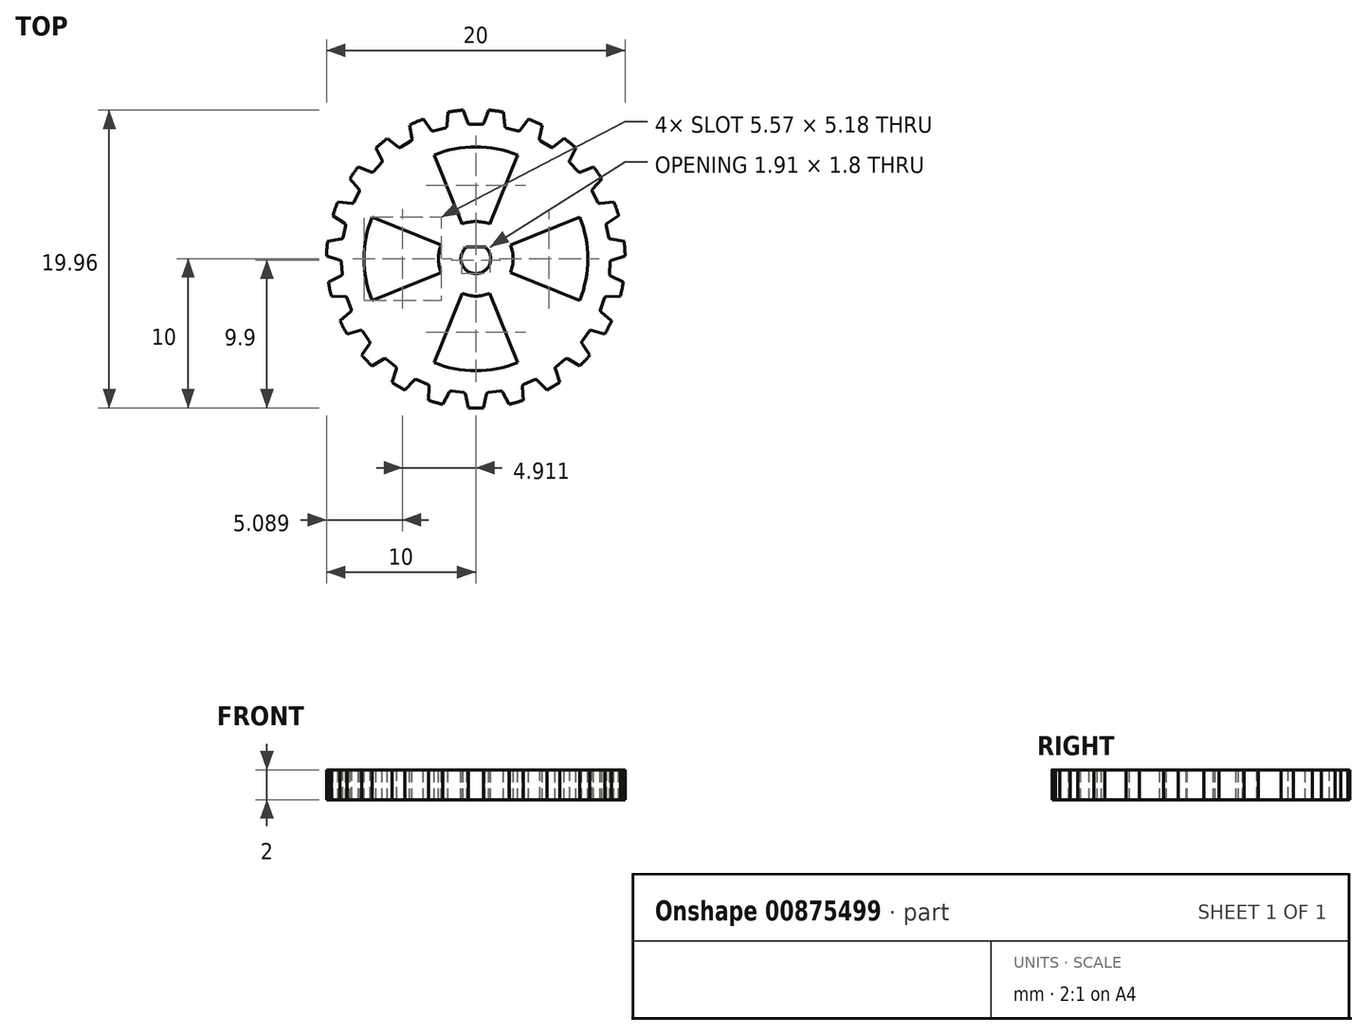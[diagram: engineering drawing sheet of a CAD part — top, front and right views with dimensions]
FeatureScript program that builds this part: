
annotation { "Feature Type Name" : "Feature", "Feature Type Description" : "" }
export const myFeature = defineFeature(function(context is Context, id is Id, definition is map)
    precondition{}
    {
        {
            var Q0;
            Q0=qCreatedBy(makeId("Top.planeOp"),FACE);
            var sketch = newSketch(context, id + "F0", { "sketchPlane" : qUnion([Q0])});
            skCircle(sketch, "E0", {"center": v(0, 0) * mm, "radius": 10 * mm});
            skSolve(sketch);
        }
        {
            var Q0;
            Q0=qSketchRegion(id+"F0",true);
            extrude(context, id + "F1", {"entities" : qUnion([Q0]), "depth" : 2 * mm, "offsetDistance" : 25 * mm});
        }
        {
            var Q0;
            Q0=makeQuery(id+"F1.opExtrude","CAP_FACE",FACE,{"disambiguationData":[OSD([sQuery(id+"F0.wireOp",EDGE,"E0")])],"isStart":false});
            var sketch = newSketch(context, id + "F2", { "sketchPlane" : qUnion([Q0])});
            skLineSegment(sketch, "E1", {"start": v(0, 0) * mm, "end": v(0, 9) * mm});
            skLineSegment(sketch, "E2", {"start": v(0, 9) * mm, "end": v(0.5, 9) * mm});
            skLineSegment(sketch, "E3", {"start": v(0, 9) * mm, "end": v(0, 10) * mm});
            skLineSegment(sketch, "E4", {"start": v(0, 10) * mm, "end": v(0.88, 10) * mm});
            skLineSegment(sketch, "E5", {"start": v(0.88, 10) * mm, "end": v(0.5, 9) * mm});
            skLineSegment(sketch, "E6.MirrorCS", {"start": v(0, 10) * mm, "end": v(-0.88, 10) * mm});
            skLineSegment(sketch, "E7.MirrorCS", {"start": v(-0.88, 10) * mm, "end": v(-0.5, 9) * mm});
            skLineSegment(sketch, "E8.MirrorCS", {"start": v(0, 9) * mm, "end": v(-0.5, 9) * mm});
            skSolve(sketch);
        }
        {
            var Q0;
            {var subQ0=sQuery(id+"F2.wireOp",EDGE,"E2");Q0=makeQuery(id+"F2.imprint","IMPRINT",FACE,{"disambiguationData":[TD([[makeQuery(id+"F2.imprint","IMPRINT",EDGE,{"derivedFrom":subQ0}),1.0]])]});}
            var Q1;
            {var subQ0=sQuery(id+"F2.wireOp",EDGE,"E3");Q1=makeQuery(id+"F2.imprint","IMPRINT",FACE,{"disambiguationData":[TD([[makeQuery(id+"F2.imprint","IMPRINT",EDGE,{"derivedFrom":subQ0}),1.0]])]});}
            extrude(context, id + "F3", {"entities" : qUnion([Q0, Q1]), "operationType" : NewBodyOperationType.REMOVE, "oppositeDirection" : true, "depth" : 25 * mm, "offsetDistance" : 25 * mm});
        }
        {
            var Q0;
            Q0=makeQuery(id+"F3.boolean.opBoolean","COPY",FACE,{"derivedFrom":makeQuery(id+"F3.opExtrude","SWEPT_FACE",FACE,{"disambiguationData":[OSD([sQuery(id+"F2.wireOp",EDGE,"E5")])]})});
            var Q1;
            Q1=makeQuery(id+"F3.boolean.opBoolean","COPY",FACE,{"derivedFrom":makeQuery(id+"F3.opExtrude","SWEPT_FACE",FACE,{"disambiguationData":[OSD([sQuery(id+"F2.wireOp",EDGE,"E2"),sQuery(id+"F2.wireOp",EDGE,"E8.MirrorCS")])]})});
            var Q2;
            Q2=makeQuery(id+"F3.boolean.opBoolean","COPY",FACE,{"derivedFrom":makeQuery(id+"F3.opExtrude","SWEPT_FACE",FACE,{"disambiguationData":[OSD([sQuery(id+"F2.wireOp",EDGE,"E7.MirrorCS")])]})});
            var Q3;
            Q3=makeQuery(id+"F1.opExtrude","SWEPT_FACE",FACE,{"disambiguationData":[OSD([sQuery(id+"F0.wireOp",EDGE,"E0")])]});
            circularPattern(context, id + "F4", {"patternType" : PatternType.FACE, "faces" : qUnion([Q0, Q1, Q2]), "axis" : qUnion([Q3]), "angle" : 360 * degree, "instanceCount" : 23, "equalSpace" : true});
        }
        {
            var Q0;
            Q0=makeQuery(id+"F3.boolean.opBoolean","COPY",EDGE,{"derivedFrom":makeQuery(id+"F3.opExtrude","SWEPT_EDGE",EDGE,{"disambiguationData":[OSD([sQuery(id+"F2.wireOp",EDGE,"E2"),sQuery(id+"F2.wireOp",EDGE,"E5")])]})});
            var Q1;
            Q1=makeQuery(id+"F3.boolean.opBoolean","COPY",EDGE,{"derivedFrom":makeQuery(id+"F3.opExtrude","SWEPT_EDGE",EDGE,{"disambiguationData":[OSD([sQuery(id+"F2.wireOp",EDGE,"E7.MirrorCS"),sQuery(id+"F2.wireOp",EDGE,"E8.MirrorCS")])]})});
            var Q2;
            Q2=makeQuery(id+"F3.boolean.opBoolean","COPY",EDGE,{"derivedFrom":makeQuery(id+"F3.opExtrude","SWEPT_EDGE",EDGE,{"disambiguationData":[OSD([sQuery(id+"F0.wireOp",EDGE,"E0"),sQuery(id+"F2.wireOp",EDGE,"E5")])]})});
            var Q3;
            Q3=makeQuery(id+"F3.boolean.opBoolean","COPY",EDGE,{"derivedFrom":makeQuery(id+"F3.opExtrude","SWEPT_EDGE",EDGE,{"disambiguationData":[OSD([sQuery(id+"F0.wireOp",EDGE,"E0"),sQuery(id+"F2.wireOp",EDGE,"E7.MirrorCS")])]})});
            fillet(context, id + "F5", {"entities" : qUnion([Q0, Q1, Q2, Q3]), "radius" : .15 * mm, "tangentPropagation" : true, "allowEdgeOverflow" : false});
        }
        {
            var Q0;
            Q0=makeQuery(id+"F4.opPattern","COPY",EDGE,{"derivedFrom":makeQuery(id+"F3.boolean.opBoolean","COPY",EDGE,{"derivedFrom":makeQuery(id+"F3.opExtrude","SWEPT_EDGE",EDGE,{"disambiguationData":[OSD([sQuery(id+"F0.wireOp",EDGE,"E0"),sQuery(id+"F2.wireOp",EDGE,"E5")])]})}),"instanceName":"22"});
            var Q1;
            Q1=makeQuery(id+"F4.opPattern","COPY",EDGE,{"derivedFrom":makeQuery(id+"F3.boolean.opBoolean","COPY",EDGE,{"derivedFrom":makeQuery(id+"F3.opExtrude","SWEPT_EDGE",EDGE,{"disambiguationData":[OSD([sQuery(id+"F2.wireOp",EDGE,"E2"),sQuery(id+"F2.wireOp",EDGE,"E5")])]})}),"instanceName":"22"});
            var Q2;
            Q2=makeQuery(id+"F4.opPattern","COPY",EDGE,{"derivedFrom":makeQuery(id+"F3.boolean.opBoolean","COPY",EDGE,{"derivedFrom":makeQuery(id+"F3.opExtrude","SWEPT_EDGE",EDGE,{"disambiguationData":[OSD([sQuery(id+"F2.wireOp",EDGE,"E7.MirrorCS"),sQuery(id+"F2.wireOp",EDGE,"E8.MirrorCS")])]})}),"instanceName":"22"});
            var Q3;
            Q3=makeQuery(id+"F4.opPattern","COPY",EDGE,{"derivedFrom":makeQuery(id+"F3.boolean.opBoolean","COPY",EDGE,{"derivedFrom":makeQuery(id+"F3.opExtrude","SWEPT_EDGE",EDGE,{"disambiguationData":[OSD([sQuery(id+"F0.wireOp",EDGE,"E0"),sQuery(id+"F2.wireOp",EDGE,"E7.MirrorCS")])]})}),"instanceName":"22"});
            var Q4;
            Q4=makeQuery(id+"F4.opPattern","COPY",EDGE,{"derivedFrom":makeQuery(id+"F3.boolean.opBoolean","COPY",EDGE,{"derivedFrom":makeQuery(id+"F3.opExtrude","SWEPT_EDGE",EDGE,{"disambiguationData":[OSD([sQuery(id+"F0.wireOp",EDGE,"E0"),sQuery(id+"F2.wireOp",EDGE,"E5")])]})}),"instanceName":"21"});
            var Q5;
            Q5=makeQuery(id+"F4.opPattern","COPY",EDGE,{"derivedFrom":makeQuery(id+"F3.boolean.opBoolean","COPY",EDGE,{"derivedFrom":makeQuery(id+"F3.opExtrude","SWEPT_EDGE",EDGE,{"disambiguationData":[OSD([sQuery(id+"F2.wireOp",EDGE,"E2"),sQuery(id+"F2.wireOp",EDGE,"E5")])]})}),"instanceName":"21"});
            var Q6;
            Q6=makeQuery(id+"F4.opPattern","COPY",EDGE,{"derivedFrom":makeQuery(id+"F3.boolean.opBoolean","COPY",EDGE,{"derivedFrom":makeQuery(id+"F3.opExtrude","SWEPT_EDGE",EDGE,{"disambiguationData":[OSD([sQuery(id+"F2.wireOp",EDGE,"E7.MirrorCS"),sQuery(id+"F2.wireOp",EDGE,"E8.MirrorCS")])]})}),"instanceName":"21"});
            var Q7;
            Q7=makeQuery(id+"F4.opPattern","COPY",EDGE,{"derivedFrom":makeQuery(id+"F3.boolean.opBoolean","COPY",EDGE,{"derivedFrom":makeQuery(id+"F3.opExtrude","SWEPT_EDGE",EDGE,{"disambiguationData":[OSD([sQuery(id+"F0.wireOp",EDGE,"E0"),sQuery(id+"F2.wireOp",EDGE,"E7.MirrorCS")])]})}),"instanceName":"21"});
            var Q8;
            Q8=makeQuery(id+"F4.opPattern","COPY",EDGE,{"derivedFrom":makeQuery(id+"F3.boolean.opBoolean","COPY",EDGE,{"derivedFrom":makeQuery(id+"F3.opExtrude","SWEPT_EDGE",EDGE,{"disambiguationData":[OSD([sQuery(id+"F0.wireOp",EDGE,"E0"),sQuery(id+"F2.wireOp",EDGE,"E5")])]})}),"instanceName":"20"});
            var Q9;
            Q9=makeQuery(id+"F4.opPattern","COPY",EDGE,{"derivedFrom":makeQuery(id+"F3.boolean.opBoolean","COPY",EDGE,{"derivedFrom":makeQuery(id+"F3.opExtrude","SWEPT_EDGE",EDGE,{"disambiguationData":[OSD([sQuery(id+"F2.wireOp",EDGE,"E2"),sQuery(id+"F2.wireOp",EDGE,"E5")])]})}),"instanceName":"20"});
            var Q10;
            Q10=makeQuery(id+"F4.opPattern","COPY",EDGE,{"derivedFrom":makeQuery(id+"F3.boolean.opBoolean","COPY",EDGE,{"derivedFrom":makeQuery(id+"F3.opExtrude","SWEPT_EDGE",EDGE,{"disambiguationData":[OSD([sQuery(id+"F2.wireOp",EDGE,"E7.MirrorCS"),sQuery(id+"F2.wireOp",EDGE,"E8.MirrorCS")])]})}),"instanceName":"20"});
            var Q11;
            Q11=makeQuery(id+"F4.opPattern","COPY",EDGE,{"derivedFrom":makeQuery(id+"F3.boolean.opBoolean","COPY",EDGE,{"derivedFrom":makeQuery(id+"F3.opExtrude","SWEPT_EDGE",EDGE,{"disambiguationData":[OSD([sQuery(id+"F0.wireOp",EDGE,"E0"),sQuery(id+"F2.wireOp",EDGE,"E7.MirrorCS")])]})}),"instanceName":"20"});
            var Q12;
            Q12=makeQuery(id+"F4.opPattern","COPY",EDGE,{"derivedFrom":makeQuery(id+"F3.boolean.opBoolean","COPY",EDGE,{"derivedFrom":makeQuery(id+"F3.opExtrude","SWEPT_EDGE",EDGE,{"disambiguationData":[OSD([sQuery(id+"F0.wireOp",EDGE,"E0"),sQuery(id+"F2.wireOp",EDGE,"E5")])]})}),"instanceName":"19"});
            var Q13;
            Q13=makeQuery(id+"F4.opPattern","COPY",EDGE,{"derivedFrom":makeQuery(id+"F3.boolean.opBoolean","COPY",EDGE,{"derivedFrom":makeQuery(id+"F3.opExtrude","SWEPT_EDGE",EDGE,{"disambiguationData":[OSD([sQuery(id+"F2.wireOp",EDGE,"E2"),sQuery(id+"F2.wireOp",EDGE,"E5")])]})}),"instanceName":"19"});
            var Q14;
            Q14=makeQuery(id+"F4.opPattern","COPY",EDGE,{"derivedFrom":makeQuery(id+"F3.boolean.opBoolean","COPY",EDGE,{"derivedFrom":makeQuery(id+"F3.opExtrude","SWEPT_EDGE",EDGE,{"disambiguationData":[OSD([sQuery(id+"F2.wireOp",EDGE,"E7.MirrorCS"),sQuery(id+"F2.wireOp",EDGE,"E8.MirrorCS")])]})}),"instanceName":"19"});
            var Q15;
            Q15=makeQuery(id+"F4.opPattern","COPY",EDGE,{"derivedFrom":makeQuery(id+"F3.boolean.opBoolean","COPY",EDGE,{"derivedFrom":makeQuery(id+"F3.opExtrude","SWEPT_EDGE",EDGE,{"disambiguationData":[OSD([sQuery(id+"F0.wireOp",EDGE,"E0"),sQuery(id+"F2.wireOp",EDGE,"E7.MirrorCS")])]})}),"instanceName":"19"});
            fillet(context, id + "F6", {"entities" : qUnion([Q0, Q1, Q2, Q3, Q4, Q5, Q6, Q7, Q8, Q9, Q10, Q11, Q12, Q13, Q14, Q15]), "radius" : .15 * mm, "tangentPropagation" : true, "allowEdgeOverflow" : false});
        }
        {
            var Q0;
            Q0=makeQuery(id+"F4.opPattern","COPY",EDGE,{"derivedFrom":makeQuery(id+"F3.boolean.opBoolean","COPY",EDGE,{"derivedFrom":makeQuery(id+"F3.opExtrude","SWEPT_EDGE",EDGE,{"disambiguationData":[OSD([sQuery(id+"F0.wireOp",EDGE,"E0"),sQuery(id+"F2.wireOp",EDGE,"E7.MirrorCS")])]})}),"instanceName":"1"});
            var Q1;
            Q1=makeQuery(id+"F4.opPattern","COPY",EDGE,{"derivedFrom":makeQuery(id+"F3.boolean.opBoolean","COPY",EDGE,{"derivedFrom":makeQuery(id+"F3.opExtrude","SWEPT_EDGE",EDGE,{"disambiguationData":[OSD([sQuery(id+"F2.wireOp",EDGE,"E7.MirrorCS"),sQuery(id+"F2.wireOp",EDGE,"E8.MirrorCS")])]})}),"instanceName":"1"});
            var Q2;
            Q2=makeQuery(id+"F4.opPattern","COPY",EDGE,{"derivedFrom":makeQuery(id+"F3.boolean.opBoolean","COPY",EDGE,{"derivedFrom":makeQuery(id+"F3.opExtrude","SWEPT_EDGE",EDGE,{"disambiguationData":[OSD([sQuery(id+"F2.wireOp",EDGE,"E2"),sQuery(id+"F2.wireOp",EDGE,"E5")])]})}),"instanceName":"1"});
            var Q3;
            Q3=makeQuery(id+"F4.opPattern","COPY",EDGE,{"derivedFrom":makeQuery(id+"F3.boolean.opBoolean","COPY",EDGE,{"derivedFrom":makeQuery(id+"F3.opExtrude","SWEPT_EDGE",EDGE,{"disambiguationData":[OSD([sQuery(id+"F0.wireOp",EDGE,"E0"),sQuery(id+"F2.wireOp",EDGE,"E5")])]})}),"instanceName":"1"});
            var Q4;
            Q4=makeQuery(id+"F4.opPattern","COPY",EDGE,{"derivedFrom":makeQuery(id+"F3.boolean.opBoolean","COPY",EDGE,{"derivedFrom":makeQuery(id+"F3.opExtrude","SWEPT_EDGE",EDGE,{"disambiguationData":[OSD([sQuery(id+"F0.wireOp",EDGE,"E0"),sQuery(id+"F2.wireOp",EDGE,"E7.MirrorCS")])]})}),"instanceName":"2"});
            var Q5;
            Q5=makeQuery(id+"F4.opPattern","COPY",EDGE,{"derivedFrom":makeQuery(id+"F3.boolean.opBoolean","COPY",EDGE,{"derivedFrom":makeQuery(id+"F3.opExtrude","SWEPT_EDGE",EDGE,{"disambiguationData":[OSD([sQuery(id+"F2.wireOp",EDGE,"E2"),sQuery(id+"F2.wireOp",EDGE,"E5")])]})}),"instanceName":"2"});
            var Q6;
            Q6=makeQuery(id+"F4.opPattern","COPY",EDGE,{"derivedFrom":makeQuery(id+"F3.boolean.opBoolean","COPY",EDGE,{"derivedFrom":makeQuery(id+"F3.opExtrude","SWEPT_EDGE",EDGE,{"disambiguationData":[OSD([sQuery(id+"F2.wireOp",EDGE,"E7.MirrorCS"),sQuery(id+"F2.wireOp",EDGE,"E8.MirrorCS")])]})}),"instanceName":"2"});
            var Q7;
            Q7=makeQuery(id+"F4.opPattern","COPY",EDGE,{"derivedFrom":makeQuery(id+"F3.boolean.opBoolean","COPY",EDGE,{"derivedFrom":makeQuery(id+"F3.opExtrude","SWEPT_EDGE",EDGE,{"disambiguationData":[OSD([sQuery(id+"F0.wireOp",EDGE,"E0"),sQuery(id+"F2.wireOp",EDGE,"E5")])]})}),"instanceName":"2"});
            var Q8;
            Q8=makeQuery(id+"F4.opPattern","COPY",EDGE,{"derivedFrom":makeQuery(id+"F3.boolean.opBoolean","COPY",EDGE,{"derivedFrom":makeQuery(id+"F3.opExtrude","SWEPT_EDGE",EDGE,{"disambiguationData":[OSD([sQuery(id+"F0.wireOp",EDGE,"E0"),sQuery(id+"F2.wireOp",EDGE,"E7.MirrorCS")])]})}),"instanceName":"3"});
            var Q9;
            Q9=makeQuery(id+"F4.opPattern","COPY",EDGE,{"derivedFrom":makeQuery(id+"F3.boolean.opBoolean","COPY",EDGE,{"derivedFrom":makeQuery(id+"F3.opExtrude","SWEPT_EDGE",EDGE,{"disambiguationData":[OSD([sQuery(id+"F2.wireOp",EDGE,"E7.MirrorCS"),sQuery(id+"F2.wireOp",EDGE,"E8.MirrorCS")])]})}),"instanceName":"3"});
            var Q10;
            Q10=makeQuery(id+"F4.opPattern","COPY",EDGE,{"derivedFrom":makeQuery(id+"F3.boolean.opBoolean","COPY",EDGE,{"derivedFrom":makeQuery(id+"F3.opExtrude","SWEPT_EDGE",EDGE,{"disambiguationData":[OSD([sQuery(id+"F2.wireOp",EDGE,"E2"),sQuery(id+"F2.wireOp",EDGE,"E5")])]})}),"instanceName":"3"});
            var Q11;
            Q11=makeQuery(id+"F4.opPattern","COPY",EDGE,{"derivedFrom":makeQuery(id+"F3.boolean.opBoolean","COPY",EDGE,{"derivedFrom":makeQuery(id+"F3.opExtrude","SWEPT_EDGE",EDGE,{"disambiguationData":[OSD([sQuery(id+"F0.wireOp",EDGE,"E0"),sQuery(id+"F2.wireOp",EDGE,"E5")])]})}),"instanceName":"3"});
            var Q12;
            Q12=makeQuery(id+"F4.opPattern","COPY",EDGE,{"derivedFrom":makeQuery(id+"F3.boolean.opBoolean","COPY",EDGE,{"derivedFrom":makeQuery(id+"F3.opExtrude","SWEPT_EDGE",EDGE,{"disambiguationData":[OSD([sQuery(id+"F0.wireOp",EDGE,"E0"),sQuery(id+"F2.wireOp",EDGE,"E7.MirrorCS")])]})}),"instanceName":"4"});
            var Q13;
            Q13=makeQuery(id+"F4.opPattern","COPY",EDGE,{"derivedFrom":makeQuery(id+"F3.boolean.opBoolean","COPY",EDGE,{"derivedFrom":makeQuery(id+"F3.opExtrude","SWEPT_EDGE",EDGE,{"disambiguationData":[OSD([sQuery(id+"F2.wireOp",EDGE,"E7.MirrorCS"),sQuery(id+"F2.wireOp",EDGE,"E8.MirrorCS")])]})}),"instanceName":"4"});
            var Q14;
            Q14=makeQuery(id+"F4.opPattern","COPY",EDGE,{"derivedFrom":makeQuery(id+"F3.boolean.opBoolean","COPY",EDGE,{"derivedFrom":makeQuery(id+"F3.opExtrude","SWEPT_EDGE",EDGE,{"disambiguationData":[OSD([sQuery(id+"F2.wireOp",EDGE,"E2"),sQuery(id+"F2.wireOp",EDGE,"E5")])]})}),"instanceName":"4"});
            var Q15;
            Q15=makeQuery(id+"F4.opPattern","COPY",EDGE,{"derivedFrom":makeQuery(id+"F3.boolean.opBoolean","COPY",EDGE,{"derivedFrom":makeQuery(id+"F3.opExtrude","SWEPT_EDGE",EDGE,{"disambiguationData":[OSD([sQuery(id+"F0.wireOp",EDGE,"E0"),sQuery(id+"F2.wireOp",EDGE,"E5")])]})}),"instanceName":"4"});
            var Q16;
            Q16=makeQuery(id+"F4.opPattern","COPY",EDGE,{"derivedFrom":makeQuery(id+"F3.boolean.opBoolean","COPY",EDGE,{"derivedFrom":makeQuery(id+"F3.opExtrude","SWEPT_EDGE",EDGE,{"disambiguationData":[OSD([sQuery(id+"F0.wireOp",EDGE,"E0"),sQuery(id+"F2.wireOp",EDGE,"E7.MirrorCS")])]})}),"instanceName":"5"});
            var Q17;
            Q17=makeQuery(id+"F4.opPattern","COPY",EDGE,{"derivedFrom":makeQuery(id+"F3.boolean.opBoolean","COPY",EDGE,{"derivedFrom":makeQuery(id+"F3.opExtrude","SWEPT_EDGE",EDGE,{"disambiguationData":[OSD([sQuery(id+"F2.wireOp",EDGE,"E7.MirrorCS"),sQuery(id+"F2.wireOp",EDGE,"E8.MirrorCS")])]})}),"instanceName":"5"});
            var Q18;
            Q18=makeQuery(id+"F4.opPattern","COPY",EDGE,{"derivedFrom":makeQuery(id+"F3.boolean.opBoolean","COPY",EDGE,{"derivedFrom":makeQuery(id+"F3.opExtrude","SWEPT_EDGE",EDGE,{"disambiguationData":[OSD([sQuery(id+"F2.wireOp",EDGE,"E2"),sQuery(id+"F2.wireOp",EDGE,"E5")])]})}),"instanceName":"5"});
            var Q19;
            Q19=makeQuery(id+"F4.opPattern","COPY",EDGE,{"derivedFrom":makeQuery(id+"F3.boolean.opBoolean","COPY",EDGE,{"derivedFrom":makeQuery(id+"F3.opExtrude","SWEPT_EDGE",EDGE,{"disambiguationData":[OSD([sQuery(id+"F0.wireOp",EDGE,"E0"),sQuery(id+"F2.wireOp",EDGE,"E5")])]})}),"instanceName":"5"});
            var Q20;
            Q20=makeQuery(id+"F4.opPattern","COPY",EDGE,{"derivedFrom":makeQuery(id+"F3.boolean.opBoolean","COPY",EDGE,{"derivedFrom":makeQuery(id+"F3.opExtrude","SWEPT_EDGE",EDGE,{"disambiguationData":[OSD([sQuery(id+"F0.wireOp",EDGE,"E0"),sQuery(id+"F2.wireOp",EDGE,"E7.MirrorCS")])]})}),"instanceName":"6"});
            var Q21;
            Q21=makeQuery(id+"F4.opPattern","COPY",EDGE,{"derivedFrom":makeQuery(id+"F3.boolean.opBoolean","COPY",EDGE,{"derivedFrom":makeQuery(id+"F3.opExtrude","SWEPT_EDGE",EDGE,{"disambiguationData":[OSD([sQuery(id+"F2.wireOp",EDGE,"E7.MirrorCS"),sQuery(id+"F2.wireOp",EDGE,"E8.MirrorCS")])]})}),"instanceName":"6"});
            var Q22;
            Q22=makeQuery(id+"F4.opPattern","COPY",EDGE,{"derivedFrom":makeQuery(id+"F3.boolean.opBoolean","COPY",EDGE,{"derivedFrom":makeQuery(id+"F3.opExtrude","SWEPT_EDGE",EDGE,{"disambiguationData":[OSD([sQuery(id+"F2.wireOp",EDGE,"E2"),sQuery(id+"F2.wireOp",EDGE,"E5")])]})}),"instanceName":"6"});
            var Q23;
            Q23=makeQuery(id+"F4.opPattern","COPY",EDGE,{"derivedFrom":makeQuery(id+"F3.boolean.opBoolean","COPY",EDGE,{"derivedFrom":makeQuery(id+"F3.opExtrude","SWEPT_EDGE",EDGE,{"disambiguationData":[OSD([sQuery(id+"F0.wireOp",EDGE,"E0"),sQuery(id+"F2.wireOp",EDGE,"E5")])]})}),"instanceName":"6"});
            var Q24;
            Q24=makeQuery(id+"F4.opPattern","COPY",EDGE,{"derivedFrom":makeQuery(id+"F3.boolean.opBoolean","COPY",EDGE,{"derivedFrom":makeQuery(id+"F3.opExtrude","SWEPT_EDGE",EDGE,{"disambiguationData":[OSD([sQuery(id+"F0.wireOp",EDGE,"E0"),sQuery(id+"F2.wireOp",EDGE,"E7.MirrorCS")])]})}),"instanceName":"7"});
            var Q25;
            Q25=makeQuery(id+"F4.opPattern","COPY",EDGE,{"derivedFrom":makeQuery(id+"F3.boolean.opBoolean","COPY",EDGE,{"derivedFrom":makeQuery(id+"F3.opExtrude","SWEPT_EDGE",EDGE,{"disambiguationData":[OSD([sQuery(id+"F2.wireOp",EDGE,"E7.MirrorCS"),sQuery(id+"F2.wireOp",EDGE,"E8.MirrorCS")])]})}),"instanceName":"7"});
            fillet(context, id + "F7", {"entities" : qUnion([Q0, Q1, Q2, Q3, Q4, Q5, Q6, Q7, Q8, Q9, Q10, Q11, Q12, Q13, Q14, Q15, Q16, Q17, Q18, Q19, Q20, Q21, Q22, Q23, Q24, Q25]), "radius" : .15 * mm, "tangentPropagation" : true, "allowEdgeOverflow" : false});
        }
        {
            var Q0;
            Q0=makeQuery(id+"F4.opPattern","COPY",EDGE,{"derivedFrom":makeQuery(id+"F3.boolean.opBoolean","COPY",EDGE,{"derivedFrom":makeQuery(id+"F3.opExtrude","SWEPT_EDGE",EDGE,{"disambiguationData":[OSD([sQuery(id+"F2.wireOp",EDGE,"E2"),sQuery(id+"F2.wireOp",EDGE,"E5")])]})}),"instanceName":"7"});
            var Q1;
            Q1=makeQuery(id+"F4.opPattern","COPY",EDGE,{"derivedFrom":makeQuery(id+"F3.boolean.opBoolean","COPY",EDGE,{"derivedFrom":makeQuery(id+"F3.opExtrude","SWEPT_EDGE",EDGE,{"disambiguationData":[OSD([sQuery(id+"F0.wireOp",EDGE,"E0"),sQuery(id+"F2.wireOp",EDGE,"E5")])]})}),"instanceName":"7"});
            var Q2;
            Q2=makeQuery(id+"F4.opPattern","COPY",EDGE,{"derivedFrom":makeQuery(id+"F3.boolean.opBoolean","COPY",EDGE,{"derivedFrom":makeQuery(id+"F3.opExtrude","SWEPT_EDGE",EDGE,{"disambiguationData":[OSD([sQuery(id+"F0.wireOp",EDGE,"E0"),sQuery(id+"F2.wireOp",EDGE,"E7.MirrorCS")])]})}),"instanceName":"8"});
            var Q3;
            Q3=makeQuery(id+"F4.opPattern","COPY",EDGE,{"derivedFrom":makeQuery(id+"F3.boolean.opBoolean","COPY",EDGE,{"derivedFrom":makeQuery(id+"F3.opExtrude","SWEPT_EDGE",EDGE,{"disambiguationData":[OSD([sQuery(id+"F2.wireOp",EDGE,"E7.MirrorCS"),sQuery(id+"F2.wireOp",EDGE,"E8.MirrorCS")])]})}),"instanceName":"8"});
            var Q4;
            Q4=makeQuery(id+"F4.opPattern","COPY",EDGE,{"derivedFrom":makeQuery(id+"F3.boolean.opBoolean","COPY",EDGE,{"derivedFrom":makeQuery(id+"F3.opExtrude","SWEPT_EDGE",EDGE,{"disambiguationData":[OSD([sQuery(id+"F2.wireOp",EDGE,"E2"),sQuery(id+"F2.wireOp",EDGE,"E5")])]})}),"instanceName":"8"});
            var Q5;
            Q5=makeQuery(id+"F4.opPattern","COPY",EDGE,{"derivedFrom":makeQuery(id+"F3.boolean.opBoolean","COPY",EDGE,{"derivedFrom":makeQuery(id+"F3.opExtrude","SWEPT_EDGE",EDGE,{"disambiguationData":[OSD([sQuery(id+"F0.wireOp",EDGE,"E0"),sQuery(id+"F2.wireOp",EDGE,"E5")])]})}),"instanceName":"8"});
            var Q6;
            Q6=makeQuery(id+"F4.opPattern","COPY",EDGE,{"derivedFrom":makeQuery(id+"F3.boolean.opBoolean","COPY",EDGE,{"derivedFrom":makeQuery(id+"F3.opExtrude","SWEPT_EDGE",EDGE,{"disambiguationData":[OSD([sQuery(id+"F0.wireOp",EDGE,"E0"),sQuery(id+"F2.wireOp",EDGE,"E7.MirrorCS")])]})}),"instanceName":"9"});
            var Q7;
            Q7=makeQuery(id+"F4.opPattern","COPY",EDGE,{"derivedFrom":makeQuery(id+"F3.boolean.opBoolean","COPY",EDGE,{"derivedFrom":makeQuery(id+"F3.opExtrude","SWEPT_EDGE",EDGE,{"disambiguationData":[OSD([sQuery(id+"F2.wireOp",EDGE,"E7.MirrorCS"),sQuery(id+"F2.wireOp",EDGE,"E8.MirrorCS")])]})}),"instanceName":"9"});
            var Q8;
            Q8=makeQuery(id+"F4.opPattern","COPY",EDGE,{"derivedFrom":makeQuery(id+"F3.boolean.opBoolean","COPY",EDGE,{"derivedFrom":makeQuery(id+"F3.opExtrude","SWEPT_EDGE",EDGE,{"disambiguationData":[OSD([sQuery(id+"F2.wireOp",EDGE,"E2"),sQuery(id+"F2.wireOp",EDGE,"E5")])]})}),"instanceName":"9"});
            var Q9;
            Q9=makeQuery(id+"F4.opPattern","COPY",EDGE,{"derivedFrom":makeQuery(id+"F3.boolean.opBoolean","COPY",EDGE,{"derivedFrom":makeQuery(id+"F3.opExtrude","SWEPT_EDGE",EDGE,{"disambiguationData":[OSD([sQuery(id+"F0.wireOp",EDGE,"E0"),sQuery(id+"F2.wireOp",EDGE,"E5")])]})}),"instanceName":"9"});
            var Q10;
            Q10=makeQuery(id+"F4.opPattern","COPY",EDGE,{"derivedFrom":makeQuery(id+"F3.boolean.opBoolean","COPY",EDGE,{"derivedFrom":makeQuery(id+"F3.opExtrude","SWEPT_EDGE",EDGE,{"disambiguationData":[OSD([sQuery(id+"F0.wireOp",EDGE,"E0"),sQuery(id+"F2.wireOp",EDGE,"E7.MirrorCS")])]})}),"instanceName":"10"});
            var Q11;
            Q11=makeQuery(id+"F4.opPattern","COPY",EDGE,{"derivedFrom":makeQuery(id+"F3.boolean.opBoolean","COPY",EDGE,{"derivedFrom":makeQuery(id+"F3.opExtrude","SWEPT_EDGE",EDGE,{"disambiguationData":[OSD([sQuery(id+"F2.wireOp",EDGE,"E7.MirrorCS"),sQuery(id+"F2.wireOp",EDGE,"E8.MirrorCS")])]})}),"instanceName":"10"});
            var Q12;
            Q12=makeQuery(id+"F4.opPattern","COPY",EDGE,{"derivedFrom":makeQuery(id+"F3.boolean.opBoolean","COPY",EDGE,{"derivedFrom":makeQuery(id+"F3.opExtrude","SWEPT_EDGE",EDGE,{"disambiguationData":[OSD([sQuery(id+"F2.wireOp",EDGE,"E2"),sQuery(id+"F2.wireOp",EDGE,"E5")])]})}),"instanceName":"10"});
            var Q13;
            Q13=makeQuery(id+"F4.opPattern","COPY",EDGE,{"derivedFrom":makeQuery(id+"F3.boolean.opBoolean","COPY",EDGE,{"derivedFrom":makeQuery(id+"F3.opExtrude","SWEPT_EDGE",EDGE,{"disambiguationData":[OSD([sQuery(id+"F0.wireOp",EDGE,"E0"),sQuery(id+"F2.wireOp",EDGE,"E5")])]})}),"instanceName":"10"});
            var Q14;
            Q14=makeQuery(id+"F4.opPattern","COPY",EDGE,{"derivedFrom":makeQuery(id+"F3.boolean.opBoolean","COPY",EDGE,{"derivedFrom":makeQuery(id+"F3.opExtrude","SWEPT_EDGE",EDGE,{"disambiguationData":[OSD([sQuery(id+"F0.wireOp",EDGE,"E0"),sQuery(id+"F2.wireOp",EDGE,"E7.MirrorCS")])]})}),"instanceName":"11"});
            var Q15;
            Q15=makeQuery(id+"F4.opPattern","COPY",EDGE,{"derivedFrom":makeQuery(id+"F3.boolean.opBoolean","COPY",EDGE,{"derivedFrom":makeQuery(id+"F3.opExtrude","SWEPT_EDGE",EDGE,{"disambiguationData":[OSD([sQuery(id+"F2.wireOp",EDGE,"E7.MirrorCS"),sQuery(id+"F2.wireOp",EDGE,"E8.MirrorCS")])]})}),"instanceName":"11"});
            var Q16;
            Q16=makeQuery(id+"F4.opPattern","COPY",EDGE,{"derivedFrom":makeQuery(id+"F3.boolean.opBoolean","COPY",EDGE,{"derivedFrom":makeQuery(id+"F3.opExtrude","SWEPT_EDGE",EDGE,{"disambiguationData":[OSD([sQuery(id+"F0.wireOp",EDGE,"E0"),sQuery(id+"F2.wireOp",EDGE,"E5")])]})}),"instanceName":"11"});
            var Q17;
            Q17=makeQuery(id+"F4.opPattern","COPY",EDGE,{"derivedFrom":makeQuery(id+"F3.boolean.opBoolean","COPY",EDGE,{"derivedFrom":makeQuery(id+"F3.opExtrude","SWEPT_EDGE",EDGE,{"disambiguationData":[OSD([sQuery(id+"F2.wireOp",EDGE,"E2"),sQuery(id+"F2.wireOp",EDGE,"E5")])]})}),"instanceName":"11"});
            var Q18;
            Q18=makeQuery(id+"F4.opPattern","COPY",EDGE,{"derivedFrom":makeQuery(id+"F3.boolean.opBoolean","COPY",EDGE,{"derivedFrom":makeQuery(id+"F3.opExtrude","SWEPT_EDGE",EDGE,{"disambiguationData":[OSD([sQuery(id+"F0.wireOp",EDGE,"E0"),sQuery(id+"F2.wireOp",EDGE,"E7.MirrorCS")])]})}),"instanceName":"12"});
            var Q19;
            Q19=makeQuery(id+"F4.opPattern","COPY",EDGE,{"derivedFrom":makeQuery(id+"F3.boolean.opBoolean","COPY",EDGE,{"derivedFrom":makeQuery(id+"F3.opExtrude","SWEPT_EDGE",EDGE,{"disambiguationData":[OSD([sQuery(id+"F2.wireOp",EDGE,"E7.MirrorCS"),sQuery(id+"F2.wireOp",EDGE,"E8.MirrorCS")])]})}),"instanceName":"12"});
            var Q20;
            Q20=makeQuery(id+"F4.opPattern","COPY",EDGE,{"derivedFrom":makeQuery(id+"F3.boolean.opBoolean","COPY",EDGE,{"derivedFrom":makeQuery(id+"F3.opExtrude","SWEPT_EDGE",EDGE,{"disambiguationData":[OSD([sQuery(id+"F2.wireOp",EDGE,"E2"),sQuery(id+"F2.wireOp",EDGE,"E5")])]})}),"instanceName":"12"});
            var Q21;
            Q21=makeQuery(id+"F4.opPattern","COPY",EDGE,{"derivedFrom":makeQuery(id+"F3.boolean.opBoolean","COPY",EDGE,{"derivedFrom":makeQuery(id+"F3.opExtrude","SWEPT_EDGE",EDGE,{"disambiguationData":[OSD([sQuery(id+"F0.wireOp",EDGE,"E0"),sQuery(id+"F2.wireOp",EDGE,"E5")])]})}),"instanceName":"12"});
            var Q22;
            Q22=makeQuery(id+"F4.opPattern","COPY",EDGE,{"derivedFrom":makeQuery(id+"F3.boolean.opBoolean","COPY",EDGE,{"derivedFrom":makeQuery(id+"F3.opExtrude","SWEPT_EDGE",EDGE,{"disambiguationData":[OSD([sQuery(id+"F0.wireOp",EDGE,"E0"),sQuery(id+"F2.wireOp",EDGE,"E7.MirrorCS")])]})}),"instanceName":"13"});
            var Q23;
            Q23=makeQuery(id+"F4.opPattern","COPY",EDGE,{"derivedFrom":makeQuery(id+"F3.boolean.opBoolean","COPY",EDGE,{"derivedFrom":makeQuery(id+"F3.opExtrude","SWEPT_EDGE",EDGE,{"disambiguationData":[OSD([sQuery(id+"F2.wireOp",EDGE,"E7.MirrorCS"),sQuery(id+"F2.wireOp",EDGE,"E8.MirrorCS")])]})}),"instanceName":"13"});
            var Q24;
            Q24=makeQuery(id+"F4.opPattern","COPY",EDGE,{"derivedFrom":makeQuery(id+"F3.boolean.opBoolean","COPY",EDGE,{"derivedFrom":makeQuery(id+"F3.opExtrude","SWEPT_EDGE",EDGE,{"disambiguationData":[OSD([sQuery(id+"F0.wireOp",EDGE,"E0"),sQuery(id+"F2.wireOp",EDGE,"E5")])]})}),"instanceName":"13"});
            var Q25;
            Q25=makeQuery(id+"F4.opPattern","COPY",EDGE,{"derivedFrom":makeQuery(id+"F3.boolean.opBoolean","COPY",EDGE,{"derivedFrom":makeQuery(id+"F3.opExtrude","SWEPT_EDGE",EDGE,{"disambiguationData":[OSD([sQuery(id+"F0.wireOp",EDGE,"E0"),sQuery(id+"F2.wireOp",EDGE,"E7.MirrorCS")])]})}),"instanceName":"14"});
            var Q26;
            Q26=makeQuery(id+"F4.opPattern","COPY",EDGE,{"derivedFrom":makeQuery(id+"F3.boolean.opBoolean","COPY",EDGE,{"derivedFrom":makeQuery(id+"F3.opExtrude","SWEPT_EDGE",EDGE,{"disambiguationData":[OSD([sQuery(id+"F2.wireOp",EDGE,"E7.MirrorCS"),sQuery(id+"F2.wireOp",EDGE,"E8.MirrorCS")])]})}),"instanceName":"14"});
            var Q27;
            Q27=makeQuery(id+"F4.opPattern","COPY",EDGE,{"derivedFrom":makeQuery(id+"F3.boolean.opBoolean","COPY",EDGE,{"derivedFrom":makeQuery(id+"F3.opExtrude","SWEPT_EDGE",EDGE,{"disambiguationData":[OSD([sQuery(id+"F2.wireOp",EDGE,"E2"),sQuery(id+"F2.wireOp",EDGE,"E5")])]})}),"instanceName":"14"});
            var Q28;
            Q28=makeQuery(id+"F4.opPattern","COPY",EDGE,{"derivedFrom":makeQuery(id+"F3.boolean.opBoolean","COPY",EDGE,{"derivedFrom":makeQuery(id+"F3.opExtrude","SWEPT_EDGE",EDGE,{"disambiguationData":[OSD([sQuery(id+"F0.wireOp",EDGE,"E0"),sQuery(id+"F2.wireOp",EDGE,"E5")])]})}),"instanceName":"14"});
            var Q29;
            Q29=makeQuery(id+"F4.opPattern","COPY",EDGE,{"derivedFrom":makeQuery(id+"F3.boolean.opBoolean","COPY",EDGE,{"derivedFrom":makeQuery(id+"F3.opExtrude","SWEPT_EDGE",EDGE,{"disambiguationData":[OSD([sQuery(id+"F0.wireOp",EDGE,"E0"),sQuery(id+"F2.wireOp",EDGE,"E7.MirrorCS")])]})}),"instanceName":"15"});
            var Q30;
            Q30=makeQuery(id+"F4.opPattern","COPY",EDGE,{"derivedFrom":makeQuery(id+"F3.boolean.opBoolean","COPY",EDGE,{"derivedFrom":makeQuery(id+"F3.opExtrude","SWEPT_EDGE",EDGE,{"disambiguationData":[OSD([sQuery(id+"F2.wireOp",EDGE,"E2"),sQuery(id+"F2.wireOp",EDGE,"E5")])]})}),"instanceName":"15"});
            var Q31;
            Q31=makeQuery(id+"F4.opPattern","COPY",EDGE,{"derivedFrom":makeQuery(id+"F3.boolean.opBoolean","COPY",EDGE,{"derivedFrom":makeQuery(id+"F3.opExtrude","SWEPT_EDGE",EDGE,{"disambiguationData":[OSD([sQuery(id+"F0.wireOp",EDGE,"E0"),sQuery(id+"F2.wireOp",EDGE,"E5")])]})}),"instanceName":"15"});
            var Q32;
            Q32=makeQuery(id+"F4.opPattern","COPY",EDGE,{"derivedFrom":makeQuery(id+"F3.boolean.opBoolean","COPY",EDGE,{"derivedFrom":makeQuery(id+"F3.opExtrude","SWEPT_EDGE",EDGE,{"disambiguationData":[OSD([sQuery(id+"F2.wireOp",EDGE,"E2"),sQuery(id+"F2.wireOp",EDGE,"E5")])]})}),"instanceName":"16"});
            var Q33;
            Q33=makeQuery(id+"F4.opPattern","COPY",EDGE,{"derivedFrom":makeQuery(id+"F3.boolean.opBoolean","COPY",EDGE,{"derivedFrom":makeQuery(id+"F3.opExtrude","SWEPT_EDGE",EDGE,{"disambiguationData":[OSD([sQuery(id+"F0.wireOp",EDGE,"E0"),sQuery(id+"F2.wireOp",EDGE,"E5")])]})}),"instanceName":"16"});
            var Q34;
            Q34=makeQuery(id+"F4.opPattern","COPY",EDGE,{"derivedFrom":makeQuery(id+"F3.boolean.opBoolean","COPY",EDGE,{"derivedFrom":makeQuery(id+"F3.opExtrude","SWEPT_EDGE",EDGE,{"disambiguationData":[OSD([sQuery(id+"F2.wireOp",EDGE,"E2"),sQuery(id+"F2.wireOp",EDGE,"E5")])]})}),"instanceName":"17"});
            var Q35;
            Q35=makeQuery(id+"F4.opPattern","COPY",EDGE,{"derivedFrom":makeQuery(id+"F3.boolean.opBoolean","COPY",EDGE,{"derivedFrom":makeQuery(id+"F3.opExtrude","SWEPT_EDGE",EDGE,{"disambiguationData":[OSD([sQuery(id+"F0.wireOp",EDGE,"E0"),sQuery(id+"F2.wireOp",EDGE,"E5")])]})}),"instanceName":"17"});
            var Q36;
            Q36=makeQuery(id+"F4.opPattern","COPY",EDGE,{"derivedFrom":makeQuery(id+"F3.boolean.opBoolean","COPY",EDGE,{"derivedFrom":makeQuery(id+"F3.opExtrude","SWEPT_EDGE",EDGE,{"disambiguationData":[OSD([sQuery(id+"F0.wireOp",EDGE,"E0"),sQuery(id+"F2.wireOp",EDGE,"E7.MirrorCS")])]})}),"instanceName":"18"});
            var Q37;
            Q37=makeQuery(id+"F4.opPattern","COPY",EDGE,{"derivedFrom":makeQuery(id+"F3.boolean.opBoolean","COPY",EDGE,{"derivedFrom":makeQuery(id+"F3.opExtrude","SWEPT_EDGE",EDGE,{"disambiguationData":[OSD([sQuery(id+"F0.wireOp",EDGE,"E0"),sQuery(id+"F2.wireOp",EDGE,"E7.MirrorCS")])]})}),"instanceName":"16"});
            var Q38;
            Q38=makeQuery(id+"F4.opPattern","COPY",EDGE,{"derivedFrom":makeQuery(id+"F3.boolean.opBoolean","COPY",EDGE,{"derivedFrom":makeQuery(id+"F3.opExtrude","SWEPT_EDGE",EDGE,{"disambiguationData":[OSD([sQuery(id+"F0.wireOp",EDGE,"E0"),sQuery(id+"F2.wireOp",EDGE,"E7.MirrorCS")])]})}),"instanceName":"17"});
            var Q39;
            Q39=makeQuery(id+"F4.opPattern","COPY",EDGE,{"derivedFrom":makeQuery(id+"F3.boolean.opBoolean","COPY",EDGE,{"derivedFrom":makeQuery(id+"F3.opExtrude","SWEPT_EDGE",EDGE,{"disambiguationData":[OSD([sQuery(id+"F2.wireOp",EDGE,"E7.MirrorCS"),sQuery(id+"F2.wireOp",EDGE,"E8.MirrorCS")])]})}),"instanceName":"15"});
            var Q40;
            Q40=makeQuery(id+"F4.opPattern","COPY",EDGE,{"derivedFrom":makeQuery(id+"F3.boolean.opBoolean","COPY",EDGE,{"derivedFrom":makeQuery(id+"F3.opExtrude","SWEPT_EDGE",EDGE,{"disambiguationData":[OSD([sQuery(id+"F2.wireOp",EDGE,"E2"),sQuery(id+"F2.wireOp",EDGE,"E5")])]})}),"instanceName":"13"});
            var Q41;
            Q41=makeQuery(id+"F4.opPattern","COPY",EDGE,{"derivedFrom":makeQuery(id+"F3.boolean.opBoolean","COPY",EDGE,{"derivedFrom":makeQuery(id+"F3.opExtrude","SWEPT_EDGE",EDGE,{"disambiguationData":[OSD([sQuery(id+"F2.wireOp",EDGE,"E7.MirrorCS"),sQuery(id+"F2.wireOp",EDGE,"E8.MirrorCS")])]})}),"instanceName":"16"});
            var Q42;
            Q42=makeQuery(id+"F4.opPattern","COPY",EDGE,{"derivedFrom":makeQuery(id+"F3.boolean.opBoolean","COPY",EDGE,{"derivedFrom":makeQuery(id+"F3.opExtrude","SWEPT_EDGE",EDGE,{"disambiguationData":[OSD([sQuery(id+"F2.wireOp",EDGE,"E7.MirrorCS"),sQuery(id+"F2.wireOp",EDGE,"E8.MirrorCS")])]})}),"instanceName":"17"});
            var Q43;
            Q43=makeQuery(id+"F4.opPattern","COPY",EDGE,{"derivedFrom":makeQuery(id+"F3.boolean.opBoolean","COPY",EDGE,{"derivedFrom":makeQuery(id+"F3.opExtrude","SWEPT_EDGE",EDGE,{"disambiguationData":[OSD([sQuery(id+"F2.wireOp",EDGE,"E7.MirrorCS"),sQuery(id+"F2.wireOp",EDGE,"E8.MirrorCS")])]})}),"instanceName":"18"});
            var Q44;
            Q44=makeQuery(id+"F4.opPattern","COPY",EDGE,{"derivedFrom":makeQuery(id+"F3.boolean.opBoolean","COPY",EDGE,{"derivedFrom":makeQuery(id+"F3.opExtrude","SWEPT_EDGE",EDGE,{"disambiguationData":[OSD([sQuery(id+"F2.wireOp",EDGE,"E2"),sQuery(id+"F2.wireOp",EDGE,"E5")])]})}),"instanceName":"18"});
            var Q45;
            Q45=makeQuery(id+"F4.opPattern","COPY",EDGE,{"derivedFrom":makeQuery(id+"F3.boolean.opBoolean","COPY",EDGE,{"derivedFrom":makeQuery(id+"F3.opExtrude","SWEPT_EDGE",EDGE,{"disambiguationData":[OSD([sQuery(id+"F0.wireOp",EDGE,"E0"),sQuery(id+"F2.wireOp",EDGE,"E5")])]})}),"instanceName":"18"});
            fillet(context, id + "F8", {"entities" : qUnion([Q0, Q1, Q2, Q3, Q4, Q5, Q6, Q7, Q8, Q9, Q10, Q11, Q12, Q13, Q14, Q15, Q16, Q17, Q18, Q19, Q20, Q21, Q22, Q23, Q24, Q25, Q26, Q27, Q28, Q29, Q30, Q31, Q32, Q33, Q34, Q35, Q36, Q37, Q38, Q39, Q40, Q41, Q42, Q43, Q44, Q45]), "radius" : .15 * mm, "tangentPropagation" : true, "allowEdgeOverflow" : false});
        }
        {
            var Q0;
            Q0=makeQuery(id+"F1.opExtrude","CAP_FACE",FACE,{"disambiguationData":[OSD([sQuery(id+"F0.wireOp",EDGE,"E0")])],"isStart":false});
            var sketch = newSketch(context, id + "F9", { "sketchPlane" : qUnion([Q0])});
            skCircle(sketch, "E9", {"center": v(0, 0) * mm, "radius": 1 * mm});
            skLineSegment(sketch, "E10", {"start": v(0, 0) * mm, "end": v(0, 0.8) * mm});
            skLineSegment(sketch, "E11", {"start": v(0.6, 0.8) * mm, "end": v(-0.6, 0.8) * mm});
            skSolve(sketch);
        }
        {
            var Q0;
            {var subQ0=sQuery(id+"F9.wireOp",EDGE,"E11");var subQ4=makeQuery(id+"F9.imprint","IMPRINT",VERTEX,{"derivedFrom":subQ0});Q0=makeQuery(id+"F9.imprint","IMPRINT",FACE,{"disambiguationData":[TD([[makeQuery(id+"F9.imprint","IMPRINT",EDGE,{"disambiguationData":[TD([[subQ4,1.0]])],"derivedFrom":subQ0}),1.0]])]});}
            extrude(context, id + "F10", {"entities" : qUnion([Q0]), "operationType" : NewBodyOperationType.REMOVE, "oppositeDirection" : true, "depth" : 25 * mm, "offsetDistance" : 25 * mm});
        }
        {
            var Q0;
            Q0=makeQuery(id+"F1.opExtrude","CAP_FACE",FACE,{"disambiguationData":[OSD([sQuery(id+"F0.wireOp",EDGE,"E0")])],"isStart":false});
            var sketch = newSketch(context, id + "F11", { "sketchPlane" : qUnion([Q0])});
            skCircle(sketch, "E12", {"center": v(0, 0) * mm, "radius": 2.5 * mm});
            skCircle(sketch, "E13", {"center": v(0, 0) * mm, "radius": 7.5 * mm});
            skLineSegment(sketch, "E14", {"start": v(0, 7.5) * mm, "end": v(3, 7.5) * mm});
            skLineSegment(sketch, "E15", {"start": v(0, 7.5) * mm, "end": v(-3, 7.5) * mm});
            skLineSegment(sketch, "E16", {"start": v(-3, 7.5) * mm, "end": v(0, 0) * mm});
            skLineSegment(sketch, "E17", {"start": v(3, 7.5) * mm, "end": v(0, 0) * mm});
            skSolve(sketch);
        }
        {
            var Q0;
            {var subQ0=sQuery(id+"F11.wireOp",EDGE,"E16");var subQ1=sQuery(id+"F11.wireOp",EDGE,"E12");var subQ2=makeQuery(id+"F11.imprint","INTERSECT",VERTEX,{"derivedFrom":[subQ1,subQ0]});Q0=makeQuery(id+"F11.imprint","IMPRINT",FACE,{"disambiguationData":[TD([[makeQuery(id+"F11.imprint","IMPRINT",EDGE,{"disambiguationData":[TD([[subQ2,1.0]])],"derivedFrom":subQ1}),-1.0]])]});}
            extrude(context, id + "F12", {"entities" : qUnion([Q0]), "operationType" : NewBodyOperationType.REMOVE, "oppositeDirection" : true, "depth" : 25 * mm, "offsetDistance" : 25 * mm});
        }
        {
            var Q0;
            Q0=makeQuery(id+"F12.boolean.opBoolean","COPY",FACE,{"derivedFrom":makeQuery(id+"F12.opExtrude","SWEPT_FACE",FACE,{"disambiguationData":[OSD([sQuery(id+"F11.wireOp",EDGE,"E12")])]})});
            var Q1;
            Q1=makeQuery(id+"F12.boolean.opBoolean","COPY",FACE,{"derivedFrom":makeQuery(id+"F12.opExtrude","SWEPT_FACE",FACE,{"disambiguationData":[OSD([sQuery(id+"F11.wireOp",EDGE,"E16")])]})});
            var Q2;
            Q2=makeQuery(id+"F12.boolean.opBoolean","COPY",FACE,{"derivedFrom":makeQuery(id+"F12.opExtrude","SWEPT_FACE",FACE,{"disambiguationData":[OSD([sQuery(id+"F11.wireOp",EDGE,"E13")])]})});
            var Q3;
            Q3=makeQuery(id+"F12.boolean.opBoolean","COPY",FACE,{"derivedFrom":makeQuery(id+"F12.opExtrude","SWEPT_FACE",FACE,{"disambiguationData":[OSD([sQuery(id+"F11.wireOp",EDGE,"E17")])]})});
            var Q4;
            Q4=makeQuery(id+"F10.boolean.opBoolean","COPY",FACE,{"derivedFrom":makeQuery(id+"F10.opExtrude","SWEPT_FACE",FACE,{"disambiguationData":[OSD([sQuery(id+"F9.wireOp",EDGE,"E9")])]})});
            circularPattern(context, id + "F13", {"patternType" : PatternType.FACE, "faces" : qUnion([Q0, Q1, Q2, Q3]), "axis" : qUnion([Q4]), "angle" : 360 * degree, "instanceCount" : 4, "equalSpace" : true});
        }
    });
